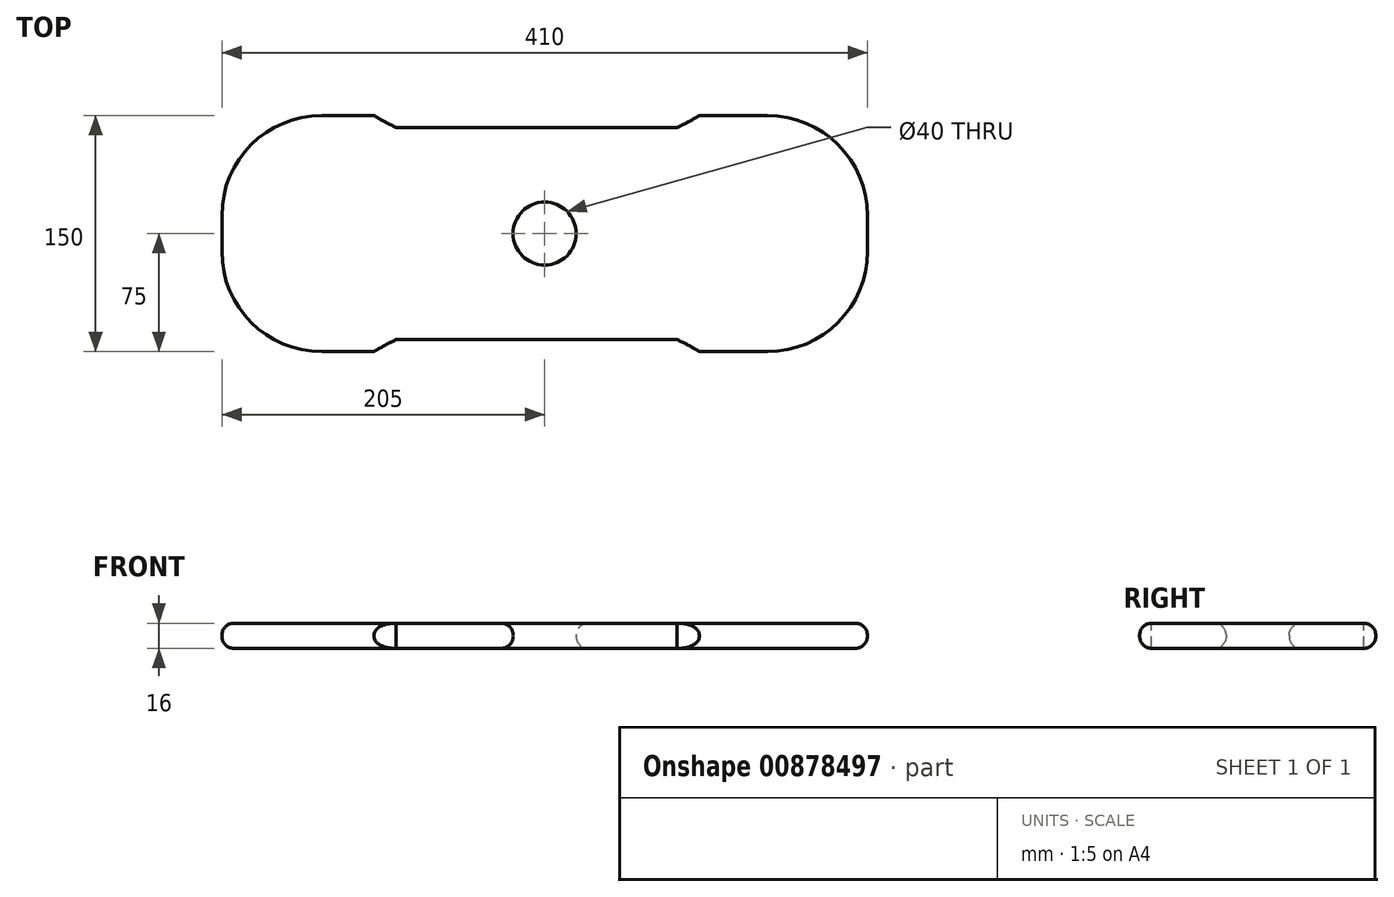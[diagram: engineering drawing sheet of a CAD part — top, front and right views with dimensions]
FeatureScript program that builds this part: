
annotation { "Feature Type Name" : "Feature", "Feature Type Description" : "" }
export const myFeature = defineFeature(function(context is Context, id is Id, definition is map)
    precondition{}
    {
        {
            var Q0;
            Q0=qCreatedBy(makeId("Top.planeOp"),FACE);
            var sketch = newSketch(context, id + "F0", { "sketchPlane" : qUnion([Q0])});
            skLineSegment(sketch, "E0.bottom", {"start": v(0, 0) * mm, "end": v(-410, 0) * mm});
            skLineSegment(sketch, "E0.top", {"start": v(0, 150) * mm, "end": v(-410, 150) * mm});
            skLineSegment(sketch, "E0.left", {"start": v(0, 0) * mm, "end": v(0, 150) * mm});
            skLineSegment(sketch, "E0.right", {"start": v(-410, 0) * mm, "end": v(-410, 150) * mm});
            skSolve(sketch);
        }
        {
            var Q0;
            Q0=makeQuery(id+"F0.imprint","IMPRINT",FACE,{"disambiguationData":[TD([[makeQuery(id+"F0.imprint","IMPRINT",EDGE,{"derivedFrom":sQuery(id+"F0.wireOp",EDGE,"E0.bottom")}),-1.0]])]});
            var Q1;
            Q1=qSketchRegion(id+"F2",true);
            extrude(context, id + "F1", {"entities" : qUnion([Q0, Q1]), "depth" : 16 * mm, "offsetDistance" : 25.4 * mm});
        }
        {
            var Q0;
            Q0=makeQuery(id+"F1.opExtrude","CAP_FACE",FACE,{"disambiguationData":[OSD([sQuery(id+"F0.wireOp",EDGE,"E0.bottom"),sQuery(id+"F0.wireOp",EDGE,"E0.top"),sQuery(id+"F0.wireOp",EDGE,"E0.left"),sQuery(id+"F0.wireOp",EDGE,"E0.right")])],"isStart":true});
            var sketch = newSketch(context, id + "F2", { "sketchPlane" : qUnion([Q0])});
            skCircle(sketch, "E1", {"center": v(-205, -75) * mm, "radius": 20 * mm});
            skSolve(sketch);
        }
        {
            var Q0;
            Q0=makeQuery(id+"F2.imprint","IMPRINT",FACE,{"disambiguationData":[TD([[makeQuery(id+"F2.imprint","IMPRINT",EDGE,{"derivedFrom":sQuery(id+"F2.wireOp",EDGE,"E1")}),1.0]])]});
            extrude(context, id + "F3", {"entities" : qUnion([Q0]), "operationType" : NewBodyOperationType.REMOVE, "endBound" : BoundingType.THROUGH_ALL, "oppositeDirection" : true, "depth" : 25.4 * mm, "offsetDistance" : 25.4 * mm});
        }
        {
            var Q0;
            Q0=makeQuery(id+"F1.opExtrude","SWEPT_EDGE",EDGE,{"disambiguationData":[OSD([sQuery(id+"F0.wireOp",EDGE,"E0.top"),sQuery(id+"F0.wireOp",EDGE,"E0.right")])]});
            var Q1;
            Q1=makeQuery(id+"F1.opExtrude","SWEPT_EDGE",EDGE,{"disambiguationData":[OSD([sQuery(id+"F0.wireOp",EDGE,"E0.bottom"),sQuery(id+"F0.wireOp",EDGE,"E0.right")])]});
            var Q2;
            Q2=makeQuery(id+"F1.opExtrude","SWEPT_EDGE",EDGE,{"disambiguationData":[OSD([sQuery(id+"F0.wireOp",EDGE,"E0.bottom"),sQuery(id+"F0.wireOp",EDGE,"E0.left")])]});
            var Q3;
            Q3=makeQuery(id+"F1.opExtrude","SWEPT_EDGE",EDGE,{"disambiguationData":[OSD([sQuery(id+"F0.wireOp",EDGE,"E0.top"),sQuery(id+"F0.wireOp",EDGE,"E0.left")])]});
            fillet(context, id + "F4", {"entities" : qUnion([Q0, Q1, Q2, Q3]), "radius" : 63.5 * mm, "tangentPropagation" : true, "allowEdgeOverflow" : false});
        }
        {
            var Q0;
            Q0=makeQuery(id+"F1.opExtrude","CAP_EDGE",EDGE,{"disambiguationData":[OSD([sQuery(id+"F0.wireOp",EDGE,"E0.bottom")])],"isStart":true});
            var Q1;
            Q1=makeQuery(id+"F1.opExtrude","CAP_EDGE",EDGE,{"disambiguationData":[OSD([sQuery(id+"F0.wireOp",EDGE,"E0.bottom")])],"isStart":false});
            var Q2;
            Q2=makeQuery(id+"F3.boolean.opBoolean","INTERSECT",EDGE,{"derivedFrom":[makeQuery(id+"F1.opExtrude","CAP_FACE",FACE,{"disambiguationData":[OSD([sQuery(id+"F0.wireOp",EDGE,"E0.bottom"),sQuery(id+"F0.wireOp",EDGE,"E0.top"),sQuery(id+"F0.wireOp",EDGE,"E0.left"),sQuery(id+"F0.wireOp",EDGE,"E0.right")])],"isStart":false}),makeQuery(id+"F3.opExtrude","SWEPT_FACE",FACE,{"disambiguationData":[OSD([sQuery(id+"F2.wireOp",EDGE,"E1")])]})]});
            var Q3;
            Q3=makeQuery(id+"F1.opExtrude","CAP_FACE",FACE,{"disambiguationData":[OSD([sQuery(id+"F0.wireOp",EDGE,"E0.bottom"),sQuery(id+"F0.wireOp",EDGE,"E0.top"),sQuery(id+"F0.wireOp",EDGE,"E0.left"),sQuery(id+"F0.wireOp",EDGE,"E0.right")])],"isStart":true});
            fillet(context, id + "F5", {"entities" : qUnion([Q0, Q1, Q2, Q3]), "radius" : 7.62 * mm, "tangentPropagation" : true, "allowEdgeOverflow" : false});
        }
        {
            var Q0;
            Q0=makeQuery(id+"F1.opExtrude","CAP_FACE",FACE,{"disambiguationData":[OSD([sQuery(id+"F0.wireOp",EDGE,"E0.bottom"),sQuery(id+"F0.wireOp",EDGE,"E0.top"),sQuery(id+"F0.wireOp",EDGE,"E0.left"),sQuery(id+"F0.wireOp",EDGE,"E0.right")])],"isStart":false});
            var sketch = newSketch(context, id + "F6", { "sketchPlane" : qUnion([Q0])});
            skEllipse(sketch, "E2", {"center": v(-210.03, -34.23) * mm, "majorRadius": 127 * mm, "minorRadius": 58.78 * mm, "majorAxis": v(-1, 0)});
            skLineSegment(sketch, "E3", {"start": v(-411.58, 75) * mm, "end": v(29.69, 75) * mm});
            skEllipse(sketch, "E4.MirrorC", {"center": v(-210.03, 184.21) * mm, "majorRadius": 127 * mm, "minorRadius": 58.78 * mm, "majorAxis": v(-1, 0)});
            skSolve(sketch);
        }
        {
            var Q0;
            {var subQ0=sQuery(id+"F6.wireOp",EDGE,"E2");var subQ1=sQuery(id+"F0.wireOp",EDGE,"E0.bottom");var subQ2=makeQuery(id+"F5.opFillet","BLEND_EDGE",EDGE,{"blendedFrom":[makeQuery(id+"F1.opExtrude","CAP_EDGE",EDGE,{"disambiguationData":[OSD([subQ1])],"isStart":false}),makeQuery(id+"F1.opExtrude","CAP_FACE",FACE,{"disambiguationData":[OSD([subQ1,sQuery(id+"F0.wireOp",EDGE,"E0.top"),sQuery(id+"F0.wireOp",EDGE,"E0.left"),sQuery(id+"F0.wireOp",EDGE,"E0.right")])],"isStart":false})],"blendedInto":[makeQuery(id+"F1.opExtrude","CAP_FACE",FACE,{"disambiguationData":[OSD([subQ1,sQuery(id+"F0.wireOp",EDGE,"E0.top"),sQuery(id+"F0.wireOp",EDGE,"E0.left"),sQuery(id+"F0.wireOp",EDGE,"E0.right")])],"isStart":false})]});var subQ3=makeQuery(id+"F6.imprint","INTERSECT",VERTEX,{"disambiguationData":[OD(0.0)],"derivedFrom":[subQ2,subQ0]});Q0=makeQuery(id+"F6.imprint","IMPRINT",FACE,{"disambiguationData":[TD([[makeQuery(id+"F6.imprint","IMPRINT",EDGE,{"disambiguationData":[TD([[subQ3,1.0]])],"derivedFrom":subQ0}),1.0]])]});}
            var Q1;
            {var subQ0=sQuery(id+"F6.wireOp",EDGE,"E4.MirrorC");var subQ1=sQuery(id+"F0.wireOp",EDGE,"E0.top");var subQ2=makeQuery(id+"F5.opFillet","BLEND_EDGE",EDGE,{"blendedFrom":[makeQuery(id+"F1.opExtrude","CAP_EDGE",EDGE,{"disambiguationData":[OSD([subQ1])],"isStart":false}),makeQuery(id+"F1.opExtrude","CAP_FACE",FACE,{"disambiguationData":[OSD([sQuery(id+"F0.wireOp",EDGE,"E0.bottom"),subQ1,sQuery(id+"F0.wireOp",EDGE,"E0.left"),sQuery(id+"F0.wireOp",EDGE,"E0.right")])],"isStart":false})],"blendedInto":[makeQuery(id+"F1.opExtrude","CAP_FACE",FACE,{"disambiguationData":[OSD([sQuery(id+"F0.wireOp",EDGE,"E0.bottom"),subQ1,sQuery(id+"F0.wireOp",EDGE,"E0.left"),sQuery(id+"F0.wireOp",EDGE,"E0.right")])],"isStart":false})]});var subQ3=makeQuery(id+"F6.imprint","INTERSECT",VERTEX,{"disambiguationData":[OD(0.0)],"derivedFrom":[subQ2,subQ0]});Q1=makeQuery(id+"F6.imprint","IMPRINT",FACE,{"disambiguationData":[TD([[makeQuery(id+"F6.imprint","IMPRINT",EDGE,{"disambiguationData":[TD([[subQ3,-1.0]])],"derivedFrom":subQ0}),1.0]])]});}
            extrude(context, id + "F7", {"entities" : qUnion([Q0, Q1]), "operationType" : NewBodyOperationType.REMOVE, "endBound" : BoundingType.THROUGH_ALL, "oppositeDirection" : true, "depth" : 25.4 * mm, "offsetDistance" : 25.4 * mm});
        }
    });
